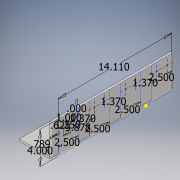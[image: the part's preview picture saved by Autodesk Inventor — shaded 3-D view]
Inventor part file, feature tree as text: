
AUTODESK INVENTOR PART (.ipt)
format: ipt  version: 2017 (Build 210142000, 142)  size: 214,528 bytes
history: native  units: in
note: dims shown in document units (in); Inventor stores cm internally (conversion verified against a paired STEP export)
features: sheet_metal_op x4, sketch x4, hole x2, other x2
ambient origin geometry x8: Origin, YZ Plane, XZ Plane, XY Plane, X Axis, Y Axis, Z Axis, Center Point
bodies: Solid1 (feature_tree)
feature tree (12):
  sheet_metal_op  "Face1"
  sheet_metal_op  "Flange1"
  hole  "Hole1"  [1 undecoded]
  hole  "Hole2"  [1 undecoded]
  sketch  "Sketch1"  dims[d0=4.0in d1=15.0in]
  other  "Plate1"
  sketch  "Sketch2"  dims[d2=0.25in d3=0.25in]
  other  "Plate2"
  sheet_metal_op  "Bend1"
  sheet_metal_op  "Corner1"
  sketch  "Sketch3"  dims[d4=0.125in]
  sketch  "Sketch4"  dims[d5=0.5in d6=0.25in d7=4.0in d8=90.0deg d9=0.001in d10=1.0in d11=0.25in d12=0.25in d13=14.11in d14=0.789in d15=4.0in d16=0.0in d17=2.5in d18=2.5in d19=1.37in d20=2.5in d21=1.37in d22=2.5in d23=1.37in d24=1.0in d25=1.25in d26=0.625in d27=0.156in d28=0.38in d29=0.332in d30=0.25in d31=0.5635in d32=0.536in d33=0.8108in d34=1.5748in d36=3.878in d37=0.3937in d39=1.0in d42=1.0in d45=3.0in d50=0.156in d51=0.38in d52=0.332in d53=0.25in d54=0.5635in d55=0.536in d56=0.8108in d58=1.375in d59=1.375in d60=2.0in d61=3.0in d62=2.0in d63=3.0in d64=1.0in d65=1.375in d66=1.375in d67=1.375in]
note: 2 required parameter values undecoded (feature->parameter linkage not recoverable at this tier; creation-order binding heuristic only, values carry confidence <= 0.55)
